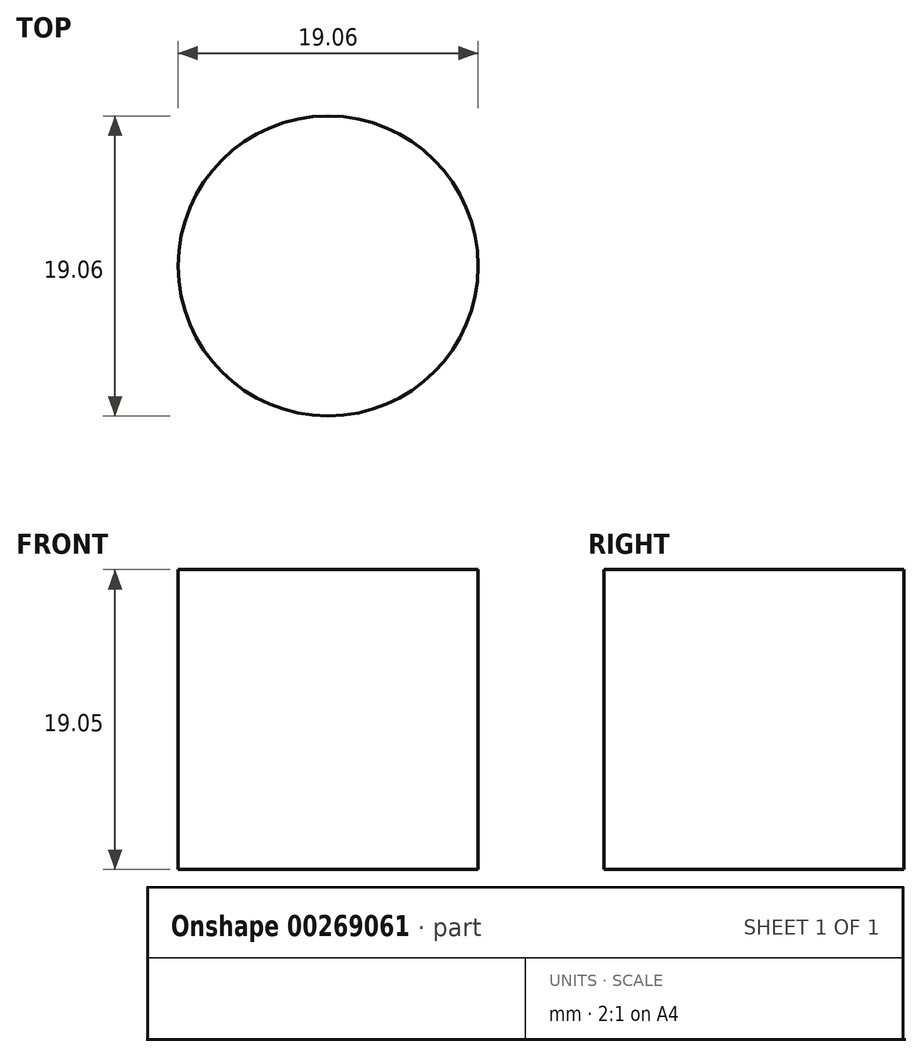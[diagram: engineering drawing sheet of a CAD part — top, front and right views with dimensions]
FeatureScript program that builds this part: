
annotation { "Feature Type Name" : "Feature", "Feature Type Description" : "" }
export const myFeature = defineFeature(function(context is Context, id is Id, definition is map)
    precondition{}
    {
        {
            var Q0;
            Q0=qCreatedBy(makeId("Top.planeOp"),FACE);
            var sketch = newSketch(context, id + "F0", { "sketchPlane" : qUnion([Q0])});
            skCircle(sketch, "E0", {"center": v(0, 0) * mm, "radius": 9.53 * mm});
            skSolve(sketch);
        }
        {
            var Q0;
            Q0 = qSketchRegion(id + "F0", true);
            extrude(context, id + "F1", {"entities" : qUnion([Q0]), "depth" : 19.05 * mm});
        }
    });
